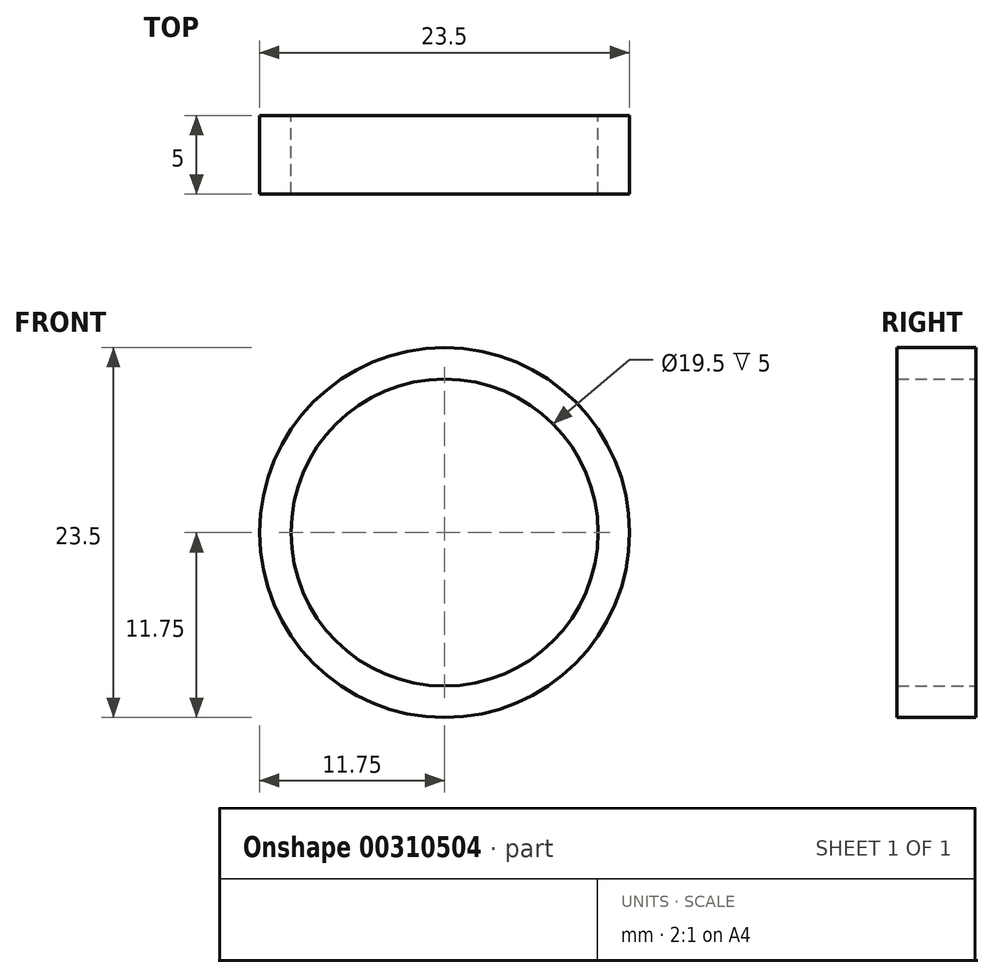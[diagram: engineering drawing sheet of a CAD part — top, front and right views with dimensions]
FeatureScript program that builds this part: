
annotation { "Feature Type Name" : "Feature", "Feature Type Description" : "" }
export const myFeature = defineFeature(function(context is Context, id is Id, definition is map)
    precondition{}
    {
        {
            var Q0;
            Q0=qCreatedBy(makeId("Front.planeOp"),FACE);
            var sketch = newSketch(context, id + "F0", { "sketchPlane" : qUnion([Q0])});
            skCircle(sketch, "E0", {"center": v(0, 0) * mm, "radius": 9.75 * mm});
            skCircle(sketch, "E1", {"center": v(0, 0) * mm, "radius": 11.75 * mm});
            skSolve(sketch);
        }
        {
            var Q0;
            Q0 = qSketchRegion(id + "F0", true);
            extrude(context, id + "F1", {"entities" : qUnion([Q0]), "depth" : 5 * mm});
        }
    });
